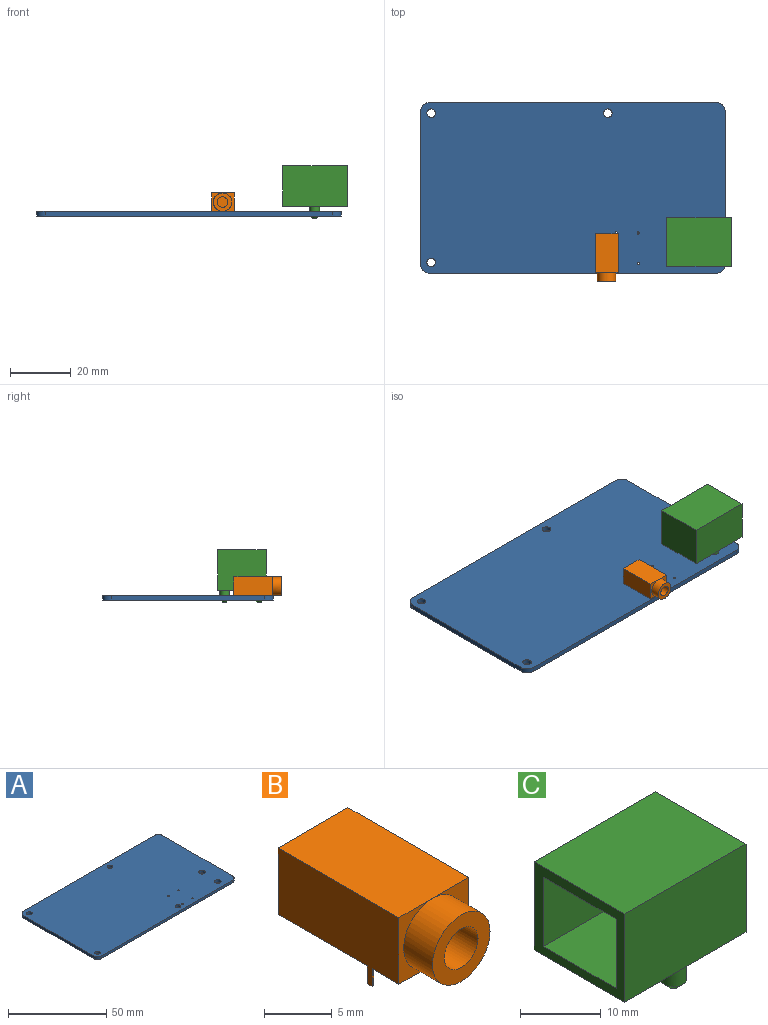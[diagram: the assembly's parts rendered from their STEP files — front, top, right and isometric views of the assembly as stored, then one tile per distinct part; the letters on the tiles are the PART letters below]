
ASSEMBLY  parts=3 mates=1
PART A: 20 faces, bbox 100x56x1.6 mm
  f0: plane 100x56mm, normal (0,0,1), area 5550.4mm2, adj f2,f3,f4,f5,f6,f7,f8,f9
  f1: plane 100x56mm, normal (0,0,-1), area 5550.4mm2, adj f2,f3,f4,f5,f6,f7,f8,f9
  f2: plane 50.4x1.6mm, normal (-1,0,0), area 80.6mm2, adj f0,f1,f10,f13
  f3: plane 94.4x1.6mm, normal (0,-1,0), area 151mm2, adj f0,f1,f10,f11
  f4: plane 50.4x1.6mm, normal (1,0,0), area 80.6mm2, adj f0,f1,f11,f12
  f5: plane 94.4x1.6mm, normal (0,1,0), area 151mm2, adj f0,f1,f12,f13
  f6: cylinder r=1.4mm len=2.8mm, axis (0,0,1), area 14.1mm2, adj f0,f1
  f7: cylinder r=1.4mm len=2.8mm, axis (0,0,1), area 14.1mm2, adj f0,f1
  f8: cylinder r=1.4mm len=2.8mm, axis (0,0,1), area 14.1mm2, adj f0,f1
  f9: cylinder r=1.4mm len=2.8mm, axis (0,0,1), area 14.1mm2, adj f0,f1
  f10: cylinder r=2.8mm len=2.8mm, axis (0,0,-1), area 7mm2, adj f0,f1,f2,f3
  f11: cylinder r=2.8mm len=2.8mm, axis (0,0,1), area 7mm2, adj f0,f1,f3,f4
  f12: cylinder r=2.8mm len=2.8mm, axis (0,0,-1), area 7mm2, adj f0,f1,f4,f5
  f13: cylinder r=2.8mm len=2.8mm, axis (0,0,1), area 7mm2, adj f0,f1,f2,f5
  f14: cylinder r=1.62mm len=3.25mm, axis (0,0,1), area 16.3mm2, adj f0,f1
  f15: cylinder r=1.62mm len=3.25mm, axis (0,0,1), area 16.3mm2, adj f0,f1
  f16: cylinder r=0.37mm len=1.6mm, axis (0,0,1), area 3.7mm2, adj f0,f1
  f17: cylinder r=0.37mm len=1.6mm, axis (0,0,1), area 3.7mm2, adj f0,f1
  f18: cylinder r=0.37mm len=1.6mm, axis (0,0,1), area 3.7mm2, adj f0,f1
  f19: cylinder r=0.37mm len=1.6mm, axis (0,0,1), area 3.7mm2, adj f0,f1
PART B: 15 faces, bbox 7.3x15.6x7.6 mm
  f0: plane 6x3.5mm, normal (0,-1,0), area 6.9mm2, adj f2,f5,f6,f8
  f1: plane 7.29x6mm, normal (0,1,0), area 43.8mm2, adj f2,f4,f5,f6
  f2: plane 12.6x7.6mm, normal (-1,0,0), area 76.4mm2, adj f0,f1,f5,f6,f11,f13,f14
  f3: plane 6x3.79mm, normal (0,-1,0), area 8.6mm2, adj f4,f5,f6,f8
  f4: plane 12.6x6mm, normal (1,0,0), area 75.6mm2, adj f1,f3,f5,f6
  f5: plane 12.6x7.29mm, normal (0,0,1), area 91.9mm2, adj f0,f1,f2,f3,f4
  f6: plane 12.6x7.29mm, normal (0,0,-1), area 91.8mm2, adj f0,f1,f2,f3,f4,f11,f12,f13
  f7: cylinder r=1.75mm len=3.5mm, axis (0,1,0), area 33mm2, adj f9,f10
  f8: cylinder r=3mm len=6mm, axis (0,1,0), area 56.5mm2, adj f0,f3,f9
  f9: plane 6x6mm, normal (0,-1,0), area 18.7mm2, adj f7,f8
  f10: plane 3.5x3.5mm, normal (0,-1,0), area 9.6mm2, adj f7
  f11: plane 1.6x0.2mm, normal (0,1,0), area 0.3mm2, adj f2,f6,f12,f14
  f12: plane 1.6x0.5mm, normal (1,0,0), area 0.8mm2, adj f6,f11,f13,f14
  f13: plane 1.6x0.2mm, normal (0,-1,0), area 0.3mm2, adj f2,f6,f12,f14
  f14: plane 0.5x0.2mm, normal (0,0,-1), area 0.1mm2, adj f2,f11,f12,f13
PART C: 17 faces, bbox 21.3x15.9x17.4 mm
  f0: plane 21.3x13.4mm, normal (0,1,0), area 285.4mm2, adj f1,f3,f4,f5
  f1: plane 15.9x13.4mm, normal (-1,0,0), area 78.5mm2, adj f0,f2,f4,f5,f12,f13,f14,f15
  f2: plane 21.3x13.4mm, normal (0,-1,0), area 285.4mm2, adj f1,f3,f4,f5
  f3: plane 15.9x13.4mm, normal (1,0,0), area 213.1mm2, adj f0,f2,f4,f5
  f4: plane 21.3x15.9mm, normal (0,0,1), area 338.7mm2, adj f0,f1,f2,f3
  f5: plane 21.3x15.9mm, normal (0,0,-1), area 322.1mm2, adj f0,f1,f2,f3,f6,f8
  f6: cylinder r=1.62mm len=3.25mm, axis (0,0,1), area 30.6mm2, adj f5,f10
  f7: plane 1.25x1.25mm, normal (0,0,-1), area 1.2mm2, adj f10
  f8: cylinder r=1.62mm len=3.25mm, axis (0,0,1), area 30.6mm2, adj f5,f11
  f9: plane 1.25x1.25mm, normal (0,0,-1), area 1.2mm2, adj f11
  f10: cone r=0.62mm half-angle=45deg, axis (0,0,1), area 10mm2, adj f6,f7
  f11: cone r=1.62mm half-angle=45deg, axis (0,0,1), area 10mm2, adj f8,f9
  f12: plane 15x10.54mm, normal (0,-1,0), area 158.1mm2, adj f1,f13,f15,f16
  f13: plane 15x12.76mm, normal (0,0,1), area 191.4mm2, adj f1,f12,f14,f16
  f14: plane 15x10.54mm, normal (0,1,0), area 158.1mm2, adj f1,f13,f15,f16
  f15: plane 15x12.76mm, normal (0,0,-1), area 191.4mm2, adj f1,f12,f14,f16
  f16: plane 12.76x10.54mm, normal (-1,0,0), area 134.5mm2, adj f12,f13,f14,f15
PLACE A t=(-54.87,47.49,7.98)mm
PLACE B t=(-51.3,23.14,9.58)mm
PLACE C rot(axis=(0,0,-1),180deg) t=(-20.92,29.74,11.18)mm
MATE slider A.f14 <-> C.f6  axis (0,0,1) through (-21.07,35.46,8.78)mm
